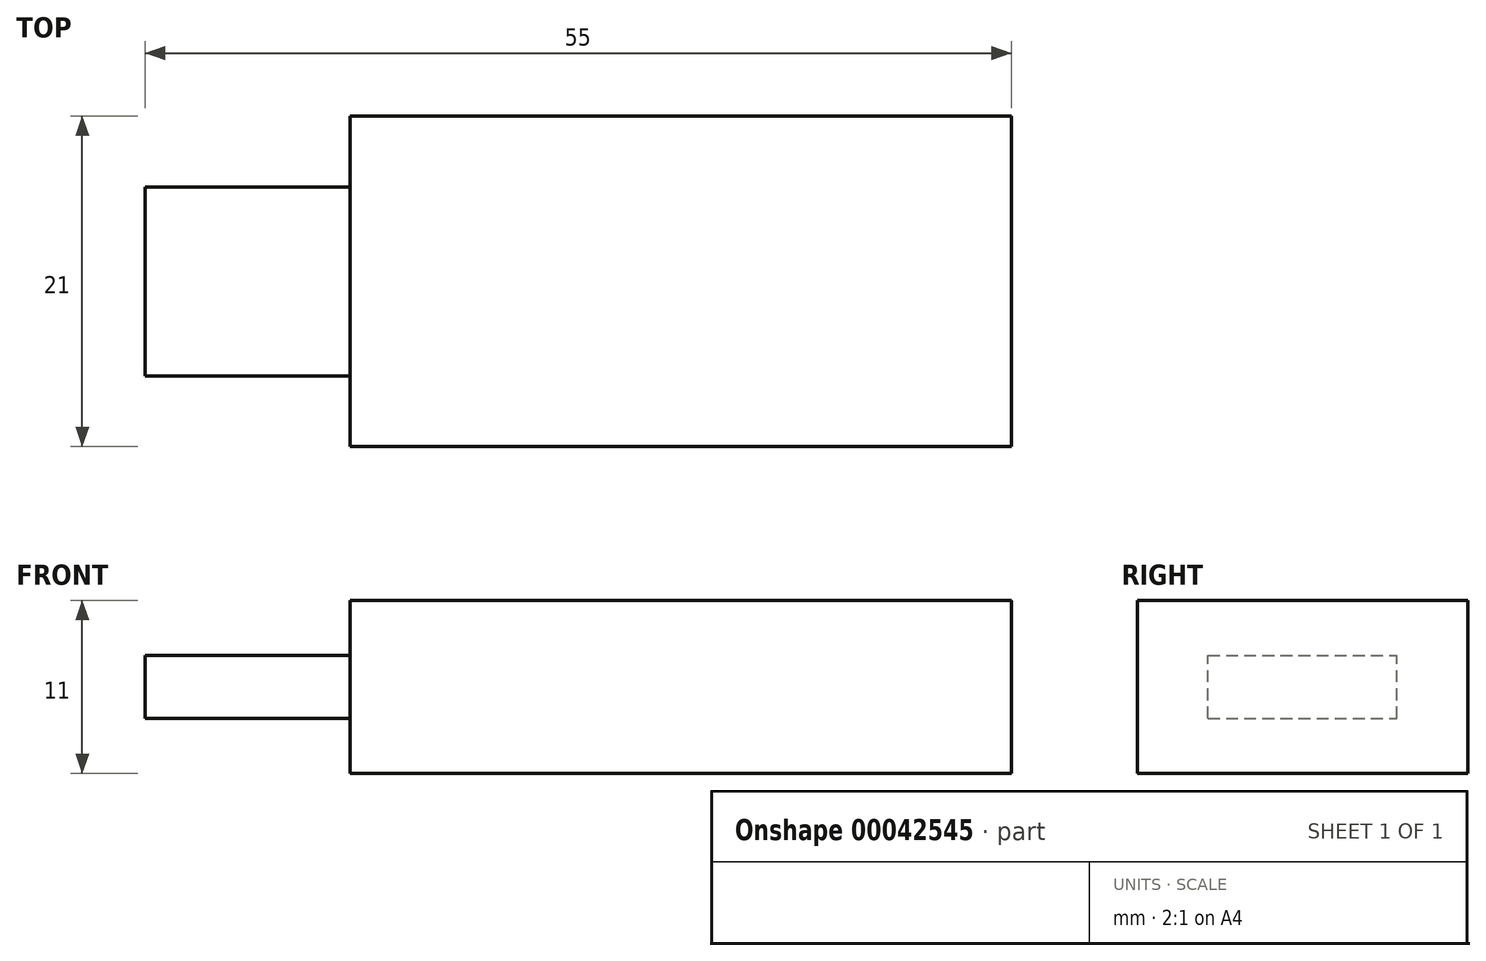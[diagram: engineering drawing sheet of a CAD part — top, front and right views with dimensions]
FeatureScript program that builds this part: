
annotation { "Feature Type Name" : "Feature", "Feature Type Description" : "" }
export const myFeature = defineFeature(function(context is Context, id is Id, definition is map)
    precondition{}
    {
        {
            var Q0;
            Q0=qCreatedBy(makeId("Top.planeOp"),FACE);
            var sketch = newSketch(context, id + "F0", { "sketchPlane" : qUnion([Q0])});
            skLineSegment(sketch, "E0.bottom", {"start": v(0, 0) * mm, "end": v(42, 0) * mm});
            skLineSegment(sketch, "E0.top", {"start": v(0, 21) * mm, "end": v(42, 21) * mm});
            skLineSegment(sketch, "E0.left", {"start": v(0, 0) * mm, "end": v(0, 21) * mm});
            skLineSegment(sketch, "E0.right", {"start": v(42, 0) * mm, "end": v(42, 21) * mm});
            skSolve(sketch);
        }
        {
            var Q0;
            Q0 = qSketchRegion(id + "F0", true);
            extrude(context, id + "F1", {"entities" : qUnion([Q0]), "depth" : 11 * mm});
        }
        {
            var Q0;
            Q0=makeQuery(id+"F1.opExtrude","SWEPT_FACE",FACE,{"disambiguationData":[OSD([sQuery(id+"F0.wireOp",EDGE,"E0.left")])]});
            var sketch = newSketch(context, id + "F2", { "sketchPlane" : qUnion([Q0])});
            skLineSegment(sketch, "E1.bottom", {"start": v(-4.5, 3.5) * mm, "end": v(-16.5, 3.5) * mm});
            skLineSegment(sketch, "E1.top", {"start": v(-4.5, 7.5) * mm, "end": v(-16.5, 7.5) * mm});
            skLineSegment(sketch, "E1.left", {"start": v(-4.5, 3.5) * mm, "end": v(-4.5, 7.5) * mm});
            skLineSegment(sketch, "E1.right", {"start": v(-16.5, 3.5) * mm, "end": v(-16.5, 7.5) * mm});
            skSolve(sketch);
        }
        {
            var Q0;
            Q0 = qSketchRegion(id + "F2", true);
            extrude(context, id + "F3", {"entities" : qUnion([Q0]), "operationType" : NewBodyOperationType.ADD, "depth" : 13 * mm});
        }
    });
